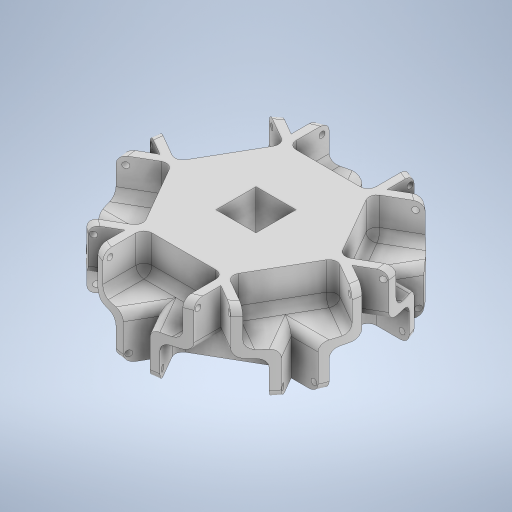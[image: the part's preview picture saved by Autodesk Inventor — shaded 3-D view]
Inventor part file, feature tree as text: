
AUTODESK INVENTOR PART (.ipt)
format: ipt  version: 2024.2 (Build 282272000, 272)  size: 747,008 bytes
history: native  units: mm
features: sketch x9, extrude x8, pattern_circular x7, fillet x6
ambient origin geometry x8: Origin, YZ Plane, XZ Plane, XY Plane, X Axis, Y Axis, Z Axis, Center Point
bodies: Solid1 (feature_tree)
feature tree (30):
  extrude  "Extrusion1"  Depth=12.0mm
  extrude  "Extrusion2"  Depth=60.0mm TaperAngle=360.0deg
  extrude  "Extrusion3"  Depth=10.0mm
  fillet  "Fillet1"  Radius=20.0mm
  pattern_circular  "Circular Pattern1"  Count=6 Angle=360.0deg
  fillet  "Fillet2"  Radius=10.0mm
  pattern_circular  "Circular Pattern2"  Count=6 Angle=360.0deg
  fillet  "Fillet3"  Radius=2.0mm
  fillet  "Fillet4"  Radius=60.0mm
  pattern_circular  "Circular Pattern3"  [2 undecoded]
  sketch  "Sketch4"  dims[d11=30.0deg d12=60.0mm d14=360.0deg d16=10.0mm d17=0.0mm]
  extrude  "Extrusion4"  TaperAngle=60.0deg  [1 undecoded]
  extrude  "Extrusion5"  Depth=10.0mm
  pattern_circular  "Circular Pattern4"  [2 undecoded]
  fillet  "Fillet5"  Radius=2.0mm
  pattern_circular  "Circular Pattern5"  [2 undecoded]
  extrude  "Extrusion6"  Depth=10.0mm TaperAngle=360.0deg
  extrude  "Extrusion7"  Depth=2.0mm
  pattern_circular  "Circular Pattern6"  Count=6 Angle=360.0deg
  fillet  "Fillet6"  Radius=2.0mm
  pattern_circular  "Circular Pattern7"  [2 undecoded]
  extrude  "Extrusion8"  TaperAngle=60.0deg  [1 undecoded]
  sketch  "Sketch1"  dims[d0=60.0mm d1=12.0mm]
  sketch  "Sketch2"  dims[d2=20.0mm d3=60.0mm d5=360.0deg]
  sketch  "Sketch3"  dims[d7=10.0mm d8=0.0mm d9=12.0mm d10=20.0mm]
  sketch  "Sketch5"  dims[d18=2.0mm d19=0.0mm]
  sketch  "Sketch6"  dims[d20=2.0mm d21=60.0mm d22=360.0deg d24=2.0mm]
  sketch  "Sketch7"  dims[d25=60.0mm d26=360.0deg d28=2.0mm d29=2.0mm d30=60.0mm d31=360.0deg]
  sketch  "Sketch8"  dims[d33=2.0mm]
  sketch  "Sketch9"  dims[d35=1.5mm d36=0.0mm d37=0.0mm d38=60.0deg d39=12.0mm d40=2.0mm d41=2.0mm d42=0.0mm d43=0.0mm d44=60.0mm d45=360.0deg d47=2.0mm d48=60.0mm d49=360.0deg d51=2.0mm d52=2.0mm d53=60.0deg d54=12.0mm d55=0.0mm d56=0.0mm d57=2.0mm d58=1.5mm d59=8.5mm d60=0.0mm d61=0.0mm d62=60.0mm d63=360.0deg d65=2.0mm d66=60.0mm d67=360.0deg d69=10.0mm d70=10.0mm d71=0.0mm d72=0.0mm d73=8.5mm d23=0.0mm]
note: 10 required parameter values undecoded (feature->parameter linkage not recoverable at this tier; creation-order binding heuristic only, values carry confidence <= 0.55)
